# Revit family: Shower_Bases-American_Standard-Townsend-6434AMFCOL
name_source: partatom
category: Plumbing Fixtures
revit_build: Autodesk Revit 2014 (Build: 20130308_1515(x64)
units: mm (PartAtom-declared; Revit-internal decimal feet)

## types (1)
- 6434AMFCOL
    ADA Compliant = Yes
    Assembly Code = D2010710
    CW Connection = No
    CWFU = 1.5
    Default Elevation = 0"
    Description = Townsend® 64" X 34" ADA Shower Base Solid Surface
    Finish = Solid Surface-American Standard-White
    HW Connection = No
    HWFU = 1.5
    Installation Type = Floor Mounted
    Length = 64"
    Manufacturer = American Standard
    Material = Solid Surface-American Standard-White
    Model = 6434AMFCOL
    Price = Prices may vary. Please consult Manufacturer Representative for most up-to-date price list.
    Product Documentation Link = https://www.americanstandard-us.com
    Product Page URL = https://www.americanstandard-us.com
    URL = https://www.americanstandard-us.com
    Vent Connection = No
    WFU = 3
    Warranty Information = Limited Lifetime warranty
    Waste Connection = Yes
    Waste Connection Diameter = 3 1/4"
    Weight (kg) = 56.2 Kg. (124 Lbs.)
    Width = 34"

## geometry (parser evidence)
native form markers: Sweep x2
no freeform markers — native parametric forms only
